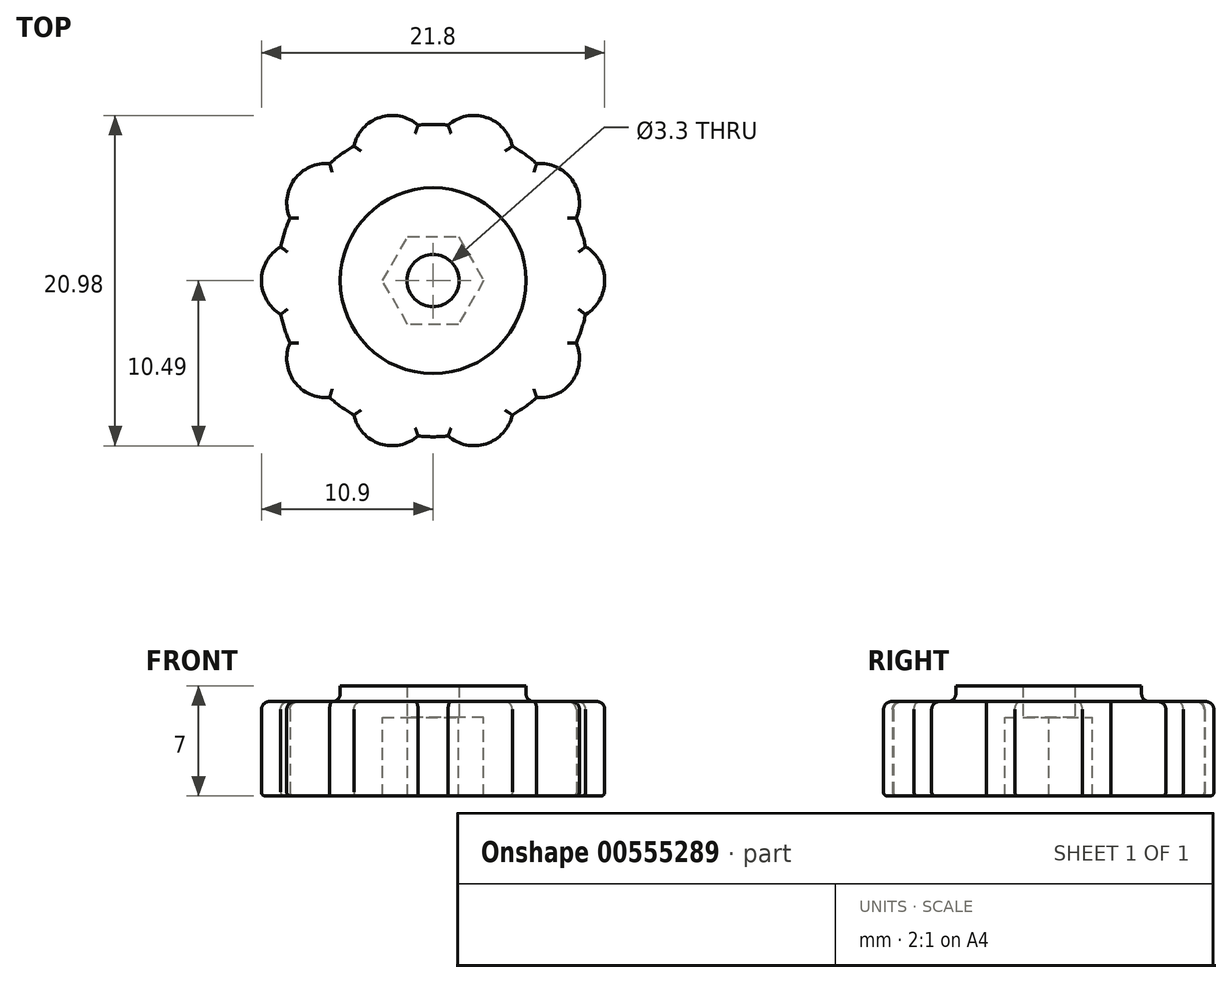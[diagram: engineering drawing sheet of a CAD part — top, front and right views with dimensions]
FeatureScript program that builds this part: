
annotation { "Feature Type Name" : "Feature", "Feature Type Description" : "" }
export const myFeature = defineFeature(function(context is Context, id is Id, definition is map)
    precondition{}
    {
        {
            var Q0;
            Q0=qCreatedBy(makeId("Top.planeOp"),FACE);
            var sketch = newSketch(context, id + "F0", { "sketchPlane" : qUnion([Q0])});
            skArc(sketch, "E0", {"start": v(-1.29, 2.14) * mm, "mid": v(-2.5, 0) * mm, "end": v(-1.29, -2.14) * mm});
            skArc(sketch, "E1.1.0", {"start": v(-0.7, -3.96) * mm, "mid": v(-0.42, -6.4) * mm, "end": v(1.82, -7.43) * mm});
            skArc(sketch, "E1.2.0", {"start": v(3.37, -8.55) * mm, "mid": v(5.03, -10.37) * mm, "end": v(7.45, -9.87) * mm});
            skArc(sketch, "E1.3.0", {"start": v(9.35, -9.87) * mm, "mid": v(11.77, -10.37) * mm, "end": v(13.43, -8.55) * mm});
            skArc(sketch, "E1.4.0", {"start": v(14.98, -7.43) * mm, "mid": v(17.22, -6.4) * mm, "end": v(17.5, -3.96) * mm});
            skArc(sketch, "E1.5.0", {"start": v(18.09, -2.14) * mm, "mid": v(19.3, 0) * mm, "end": v(18.09, 2.14) * mm});
            skArc(sketch, "E1.6.0", {"start": v(17.5, 3.96) * mm, "mid": v(17.22, 6.4) * mm, "end": v(14.98, 7.43) * mm});
            skArc(sketch, "E1.7.0", {"start": v(13.43, 8.55) * mm, "mid": v(11.77, 10.37) * mm, "end": v(9.35, 9.87) * mm});
            skArc(sketch, "E1.8.0", {"start": v(7.45, 9.87) * mm, "mid": v(5.03, 10.37) * mm, "end": v(3.37, 8.55) * mm});
            skArc(sketch, "E1.9.0", {"start": v(1.82, 7.43) * mm, "mid": v(-0.42, 6.4) * mm, "end": v(-0.7, 3.96) * mm});
            skPoint(sketch, "E1.center", {"position": v(8.4, 0) * mm});
            skArc(sketch, "E2", {"start": v(3.37, 8.55) * mm, "mid": v(2.57, 8.03) * mm, "end": v(1.82, 7.43) * mm});
            skCircle(sketch, "E3.cCircle", {"center": v(8.4, 0) * mm, "radius": 2.85 * mm, "construction": true});
            skLineSegment(sketch, "E3.0", {"start": v(10.05, -2.85) * mm, "end": v(6.75, -2.85) * mm});
            skLineSegment(sketch, "E3.1", {"start": v(6.75, -2.85) * mm, "end": v(5.1, 0) * mm});
            skLineSegment(sketch, "E3.2", {"start": v(5.1, 0) * mm, "end": v(6.75, 2.85) * mm});
            skLineSegment(sketch, "E3.3", {"start": v(6.75, 2.85) * mm, "end": v(10.05, 2.85) * mm});
            skLineSegment(sketch, "E3.4", {"start": v(10.05, 2.85) * mm, "end": v(11.7, 0) * mm});
            skLineSegment(sketch, "E3.5", {"start": v(11.7, 0) * mm, "end": v(10.05, -2.85) * mm});
            skPoint(sketch, "E3.0.midPoint", {"position": v(8.4, -2.85) * mm});
            skCircle(sketch, "E4", {"center": v(8.4, 0) * mm, "radius": 5.9 * mm});
            skArc(sketch, "E5.trimOffspring", {"start": v(-0.7, 3.96) * mm, "mid": v(-1.03, 3.07) * mm, "end": v(-1.29, 2.14) * mm});
            skArc(sketch, "E6.trimOffspring", {"start": v(-1.29, -2.14) * mm, "mid": v(-1.03, -3.07) * mm, "end": v(-0.7, -3.96) * mm});
            skArc(sketch, "E7.trimOffspring", {"start": v(1.82, -7.43) * mm, "mid": v(2.57, -8.03) * mm, "end": v(3.37, -8.55) * mm});
            skArc(sketch, "E8.trimOffspring", {"start": v(7.45, -9.87) * mm, "mid": v(8.4, -9.92) * mm, "end": v(9.35, -9.87) * mm});
            skArc(sketch, "E9.trimOffspring", {"start": v(17.5, -3.96) * mm, "mid": v(17.83, -3.07) * mm, "end": v(18.09, -2.14) * mm});
            skArc(sketch, "E10.trimOffspring", {"start": v(13.43, -8.55) * mm, "mid": v(14.23, -8.03) * mm, "end": v(14.98, -7.43) * mm});
            skArc(sketch, "E11.trimOffspring", {"start": v(18.09, 2.14) * mm, "mid": v(17.83, 3.07) * mm, "end": v(17.5, 3.96) * mm});
            skArc(sketch, "E12.trimOffspring", {"start": v(14.98, 7.43) * mm, "mid": v(14.23, 8.03) * mm, "end": v(13.43, 8.55) * mm});
            skArc(sketch, "E13.trimOffspring", {"start": v(9.35, 9.87) * mm, "mid": v(8.4, 9.92) * mm, "end": v(7.45, 9.87) * mm});
            skCircle(sketch, "E14", {"center": v(8.4, 0) * mm, "radius": 1.65 * mm});
            skSolve(sketch);
        }
        {
            var Q0;
            Q0=makeQuery(id+"F0.imprint","IMPRINT",FACE,{"disambiguationData":[TD([[makeQuery(id+"F0.imprint","IMPRINT",EDGE,{"derivedFrom":sQuery(id+"F0.wireOp",EDGE,"E0")}),1.0]])]});
            var Q1;
            Q1=makeQuery(id+"F0.imprint","IMPRINT",FACE,{"disambiguationData":[TD([[makeQuery(id+"F0.imprint","IMPRINT",EDGE,{"derivedFrom":sQuery(id+"F0.wireOp",EDGE,"E3.0")}),1.0]])]});
            var Q2;
            Q2=makeQuery(id+"F0.imprint","IMPRINT",FACE,{"disambiguationData":[TD([[makeQuery(id+"F0.imprint","IMPRINT",EDGE,{"derivedFrom":sQuery(id+"F0.wireOp",EDGE,"E3.0")}),-1.0]])]});
            extrude(context, id + "F1", {"entities" : qUnion([Q0, Q1, Q2]), "depth" : 6 * mm});
        }
        {
            var Q0;
            Q0=makeQuery(id+"F0.imprint","IMPRINT",FACE,{"disambiguationData":[TD([[makeQuery(id+"F0.imprint","IMPRINT",EDGE,{"derivedFrom":sQuery(id+"F0.wireOp",EDGE,"E3.0")}),1.0]])]});
            extrude(context, id + "F2", {"entities" : qUnion([Q0]), "operationType" : NewBodyOperationType.ADD, "depth" : 7 * mm, "offsetDistance" : 25 * mm});
        }
        {
            var Q0;
            Q0=makeQuery(id+"F0.imprint","IMPRINT",FACE,{"disambiguationData":[TD([[makeQuery(id+"F0.imprint","IMPRINT",EDGE,{"derivedFrom":sQuery(id+"F0.wireOp",EDGE,"E3.0")}),-1.0]])]});
            extrude(context, id + "F3", {"entities" : qUnion([Q0]), "operationType" : NewBodyOperationType.ADD, "depth" : 7 * mm, "offsetDistance" : 25 * mm});
        }
        {
            var Q0;
            {var subQ0=sQuery(id+"F0.wireOp",EDGE,"E3.5");var subQ1=sQuery(id+"F0.wireOp",EDGE,"E3.4");var subQ2=sQuery(id+"F0.wireOp",EDGE,"E3.3");var subQ3=sQuery(id+"F0.wireOp",EDGE,"E3.2");var subQ4=sQuery(id+"F0.wireOp",EDGE,"E3.1");var subQ5=sQuery(id+"F0.wireOp",EDGE,"E3.0");Q0=makeQuery(id+"F3.boolean.opBoolean","MERGE",FACE,{"derivedFrom":[makeQuery(id+"F2.opExtrude","CAP_FACE",FACE,{"disambiguationData":[OSD([subQ5,subQ4,subQ3,subQ2,subQ1,subQ0,sQuery(id+"F0.wireOp",EDGE,"E4")])],"isStart":false}),makeQuery(id+"F3.opExtrude","CAP_FACE",FACE,{"disambiguationData":[OSD([subQ5,subQ4,subQ3,subQ2,subQ1,subQ0,sQuery(id+"F0.wireOp",EDGE,"E14")])],"isStart":false})]});}
            var sketch = newSketch(context, id + "F4", { "sketchPlane" : qUnion([Q0])});
            skCircle(sketch, "E15.cCircle", {"center": v(8.4, 0) * mm, "radius": 2.79 * mm, "construction": true});
            skLineSegment(sketch, "E15.0", {"start": v(6.8, 2.79) * mm, "end": v(10, 2.79) * mm});
            skLineSegment(sketch, "E15.1", {"start": v(10, 2.79) * mm, "end": v(11.62, 0) * mm});
            skLineSegment(sketch, "E15.2", {"start": v(11.62, 0) * mm, "end": v(10, -2.79) * mm});
            skLineSegment(sketch, "E15.3", {"start": v(10, -2.79) * mm, "end": v(6.8, -2.79) * mm});
            skLineSegment(sketch, "E15.4", {"start": v(6.8, -2.79) * mm, "end": v(5.18, 0) * mm});
            skLineSegment(sketch, "E15.5", {"start": v(5.18, 0) * mm, "end": v(6.8, 2.79) * mm});
            skPoint(sketch, "E15.0.midPoint", {"position": v(8.4, 2.79) * mm});
            skSolve(sketch);
        }
        {
            var Q0;
            Q0=makeQuery(id+"F4.imprint","IMPRINT",FACE,{"disambiguationData":[TD([[makeQuery(id+"F4.imprint","IMPRINT",EDGE,{"derivedFrom":sQuery(id+"F4.wireOp",EDGE,"E15.0")}),-1.0]])]});
            extrude(context, id + "F5", {"entities" : qUnion([Q0]), "operationType" : NewBodyOperationType.REMOVE, "oppositeDirection" : true, "depth" : 5 * mm, "hasSecondDirection" : true, "secondDirectionOppositeDirection" : true, "secondDirectionDepth" : 2 * mm, "offsetDistance" : 25 * mm});
        }
        {
            var Q0;
            {var subQ0=sQuery(id+"F0.wireOp",EDGE,"E1.9.0");var subQ1=sQuery(id+"F0.wireOp",EDGE,"E10.trimOffspring");var subQ2=sQuery(id+"F0.wireOp",EDGE,"E1.7.0");var subQ3=sQuery(id+"F0.wireOp",EDGE,"E8.trimOffspring");var subQ4=sQuery(id+"F0.wireOp",EDGE,"E1.6.0");var subQ5=sQuery(id+"F0.wireOp",EDGE,"E1.5.0");var subQ6=sQuery(id+"F0.wireOp",EDGE,"E1.4.0");var subQ7=sQuery(id+"F0.wireOp",EDGE,"E0");var subQ8=sQuery(id+"F0.wireOp",EDGE,"E1.8.0");var subQ9=sQuery(id+"F0.wireOp",EDGE,"E9.trimOffspring");var subQ10=sQuery(id+"F0.wireOp",EDGE,"E1.1.0");var subQ11=sQuery(id+"F0.wireOp",EDGE,"E1.2.0");var subQ12=sQuery(id+"F0.wireOp",EDGE,"E1.3.0");var subQ13=sQuery(id+"F0.wireOp",EDGE,"E2");var subQ14=sQuery(id+"F0.wireOp",EDGE,"E5.trimOffspring");var subQ15=sQuery(id+"F0.wireOp",EDGE,"E11.trimOffspring");var subQ16=sQuery(id+"F0.wireOp",EDGE,"E12.trimOffspring");var subQ17=sQuery(id+"F0.wireOp",EDGE,"E6.trimOffspring");var subQ18=sQuery(id+"F0.wireOp",EDGE,"E13.trimOffspring");var subQ19=sQuery(id+"F0.wireOp",EDGE,"E7.trimOffspring");Q0=makeQuery(id+"F2.boolean.opBoolean","SPLIT",FACE,{"disambiguationData":[TD([makeQuery(id+"F1.opExtrude","SWEPT_FACE",FACE,{"disambiguationData":[OSD([subQ7])]})])],"derivedFrom":makeQuery(id+"F1.opExtrude","CAP_FACE",FACE,{"disambiguationData":[OSD([subQ7,subQ10,subQ11,subQ12,subQ6,subQ5,subQ4,subQ2,subQ8,subQ0,subQ13,subQ14,subQ17,subQ19,subQ3,subQ9,subQ1,subQ15,subQ16,subQ18,sQuery(id+"F0.wireOp",EDGE,"E14")])],"isStart":false})});}
            fillet(context, id + "F6", {"entities" : qUnion([Q0]), "radius" : 0.5 * mm, "tangentPropagation" : true, "allowEdgeOverflow" : false});
        }
        {
            var Q0;
            Q0=makeQuery(id+"F1.opExtrude","CAP_FACE",FACE,{"disambiguationData":[OSD([sQuery(id+"F0.wireOp",EDGE,"E0"),sQuery(id+"F0.wireOp",EDGE,"E1.1.0"),sQuery(id+"F0.wireOp",EDGE,"E1.2.0"),sQuery(id+"F0.wireOp",EDGE,"E1.3.0"),sQuery(id+"F0.wireOp",EDGE,"E1.4.0"),sQuery(id+"F0.wireOp",EDGE,"E1.5.0"),sQuery(id+"F0.wireOp",EDGE,"E1.6.0"),sQuery(id+"F0.wireOp",EDGE,"E1.7.0"),sQuery(id+"F0.wireOp",EDGE,"E1.8.0"),sQuery(id+"F0.wireOp",EDGE,"E1.9.0"),sQuery(id+"F0.wireOp",EDGE,"E2"),sQuery(id+"F0.wireOp",EDGE,"E5.trimOffspring"),sQuery(id+"F0.wireOp",EDGE,"E6.trimOffspring"),sQuery(id+"F0.wireOp",EDGE,"E7.trimOffspring"),sQuery(id+"F0.wireOp",EDGE,"E8.trimOffspring"),sQuery(id+"F0.wireOp",EDGE,"E9.trimOffspring"),sQuery(id+"F0.wireOp",EDGE,"E10.trimOffspring"),sQuery(id+"F0.wireOp",EDGE,"E11.trimOffspring"),sQuery(id+"F0.wireOp",EDGE,"E12.trimOffspring"),sQuery(id+"F0.wireOp",EDGE,"E13.trimOffspring"),sQuery(id+"F0.wireOp",EDGE,"E14")])],"isStart":true});
            fillet(context, id + "F7", {"entities" : qUnion([Q0]), "radius" : .25 * mm, "tangentPropagation" : true, "allowEdgeOverflow" : false});
        }
        {
            var Q0;
            Q0=makeQuery(id+"F0.imprint","IMPRINT",FACE,{"disambiguationData":[TD([[makeQuery(id+"F0.imprint","IMPRINT",EDGE,{"derivedFrom":sQuery(id+"F0.wireOp",EDGE,"E3.0")}),1.0]])]});
            var Q1;
            Q1=makeQuery(id+"F0.imprint","IMPRINT",FACE,{"disambiguationData":[TD([[makeQuery(id+"F0.imprint","IMPRINT",EDGE,{"derivedFrom":sQuery(id+"F0.wireOp",EDGE,"E3.0")}),-1.0]])]});
            extrude(context, id + "F8", {"entities" : qUnion([Q0, Q1]), "operationType" : NewBodyOperationType.REMOVE, "depth" : 2 * mm, "offsetDistance" : 25 * mm});
        }
        {
            var Q0;
            Q0=makeQuery(id+"F8.boolean.opBoolean","COPY",FACE,{"derivedFrom":makeQuery(id+"F8.opExtrude","CAP_FACE",FACE,{"disambiguationData":[OSD([sQuery(id+"F0.wireOp",EDGE,"E4"),sQuery(id+"F0.wireOp",EDGE,"E14")])],"isStart":false})});
            extrude(context, id + "F9", {"entities" : qUnion([Q0]), "operationType" : NewBodyOperationType.ADD, "depth" : 2 * mm, "offsetDistance" : 25 * mm});
        }
    });
